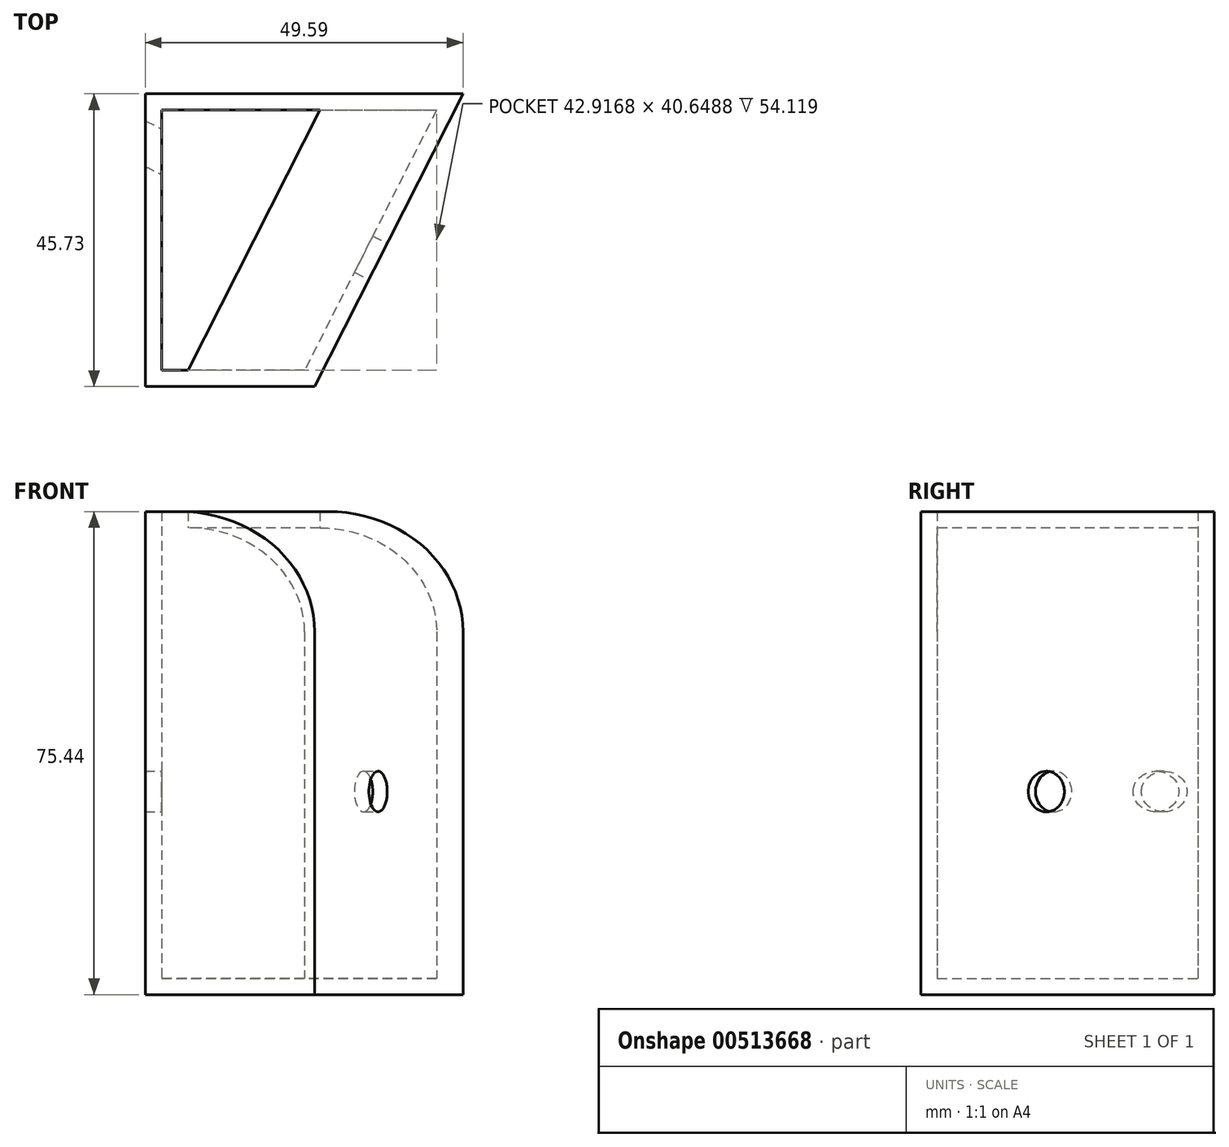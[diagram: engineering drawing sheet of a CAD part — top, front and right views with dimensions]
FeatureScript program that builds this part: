
annotation { "Feature Type Name" : "Feature", "Feature Type Description" : "" }
export const myFeature = defineFeature(function(context is Context, id is Id, definition is map)
    precondition{}
    {
        {
            var Q0;
            Q0=qCreatedBy(makeId("Top.planeOp"),FACE);
            var sketch = newSketch(context, id + "F0", { "sketchPlane" : qUnion([Q0])});
            skLineSegment(sketch, "E0", {"start": v(0, 0) * mm, "end": v(0, 45.73) * mm});
            skLineSegment(sketch, "E1", {"start": v(0, 45.73) * mm, "end": v(49.6, 45.73) * mm});
            skLineSegment(sketch, "E2", {"start": v(49.6, 45.73) * mm, "end": v(26.42, 0) * mm});
            skLineSegment(sketch, "E3", {"start": v(26.42, 0) * mm, "end": v(0, 0) * mm});
            skSolve(sketch);
        }
        {
            var Q0;
            Q0=makeQuery(id+"F0.imprint","IMPRINT",FACE,{"disambiguationData":[TD([[makeQuery(id+"F0.imprint","IMPRINT",EDGE,{"derivedFrom":sQuery(id+"F0.wireOp",EDGE,"E0")}),-1.0]])]});
            extrude(context, id + "F1", {"entities" : qUnion([Q0]), "depth" : 75.44 * mm});
        }
        {
            var Q0;
            Q0=makeQuery(id+"F1.opExtrude","CAP_EDGE",EDGE,{"disambiguationData":[OSD([sQuery(id+"F0.wireOp",EDGE,"E2")])],"isStart":false});
            fillet(context, id + "F2", {"entities" : qUnion([Q0]), "radius" : 18.78 * mm, "tangentPropagation" : true, "allowEdgeOverflow" : false});
        }
        {
            var Q0;
            Q0=makeQuery(id+"F1.opExtrude","CAP_FACE",FACE,{"disambiguationData":[OSD([sQuery(id+"F0.wireOp",EDGE,"E0"),sQuery(id+"F0.wireOp",EDGE,"E1"),sQuery(id+"F0.wireOp",EDGE,"E2"),sQuery(id+"F0.wireOp",EDGE,"E3")])],"isStart":false});
            shell(context, id + "F3", {"entities" : qUnion([Q0]), "thickness" : 2.54 * mm});
        }
        {
            var Q0;
            Q0=makeQuery(id+"F1.opExtrude","SWEPT_FACE",FACE,{"disambiguationData":[OSD([sQuery(id+"F0.wireOp",EDGE,"E2")])]});
            var sketch = newSketch(context, id + "F4", { "sketchPlane" : qUnion([Q0])});
            skPoint(sketch, "E4", {"position": v(33.85, 31.7) * mm});
            skSolve(sketch);
        }
        {
            var Q0;
            Q0=sQuery(id+"F4.wireOp",VERTEX,"E4");
            var Q1;
            Q1=makeQuery(id+"F1.opExtrude","SWEPT_BODY",BODY,{"disambiguationData":[OSD([sQuery(id+"F0.wireOp",EDGE,"E0"),sQuery(id+"F0.wireOp",EDGE,"E1"),sQuery(id+"F0.wireOp",EDGE,"E2"),sQuery(id+"F0.wireOp",EDGE,"E3")])]});
            hole(context, id + "F5", {"style" : HoleStyle.SIMPLE, "endStyle" : HoleEndStyle.THROUGH, "holeDiameter" : 6.35 * mm, "isTappedThrough" : true, "tappedDepth" : 12.7 * mm, "tapClearance" : 3, "locations" : qUnion([Q0]), "scope" : qUnion([Q1])});
        }
    });
